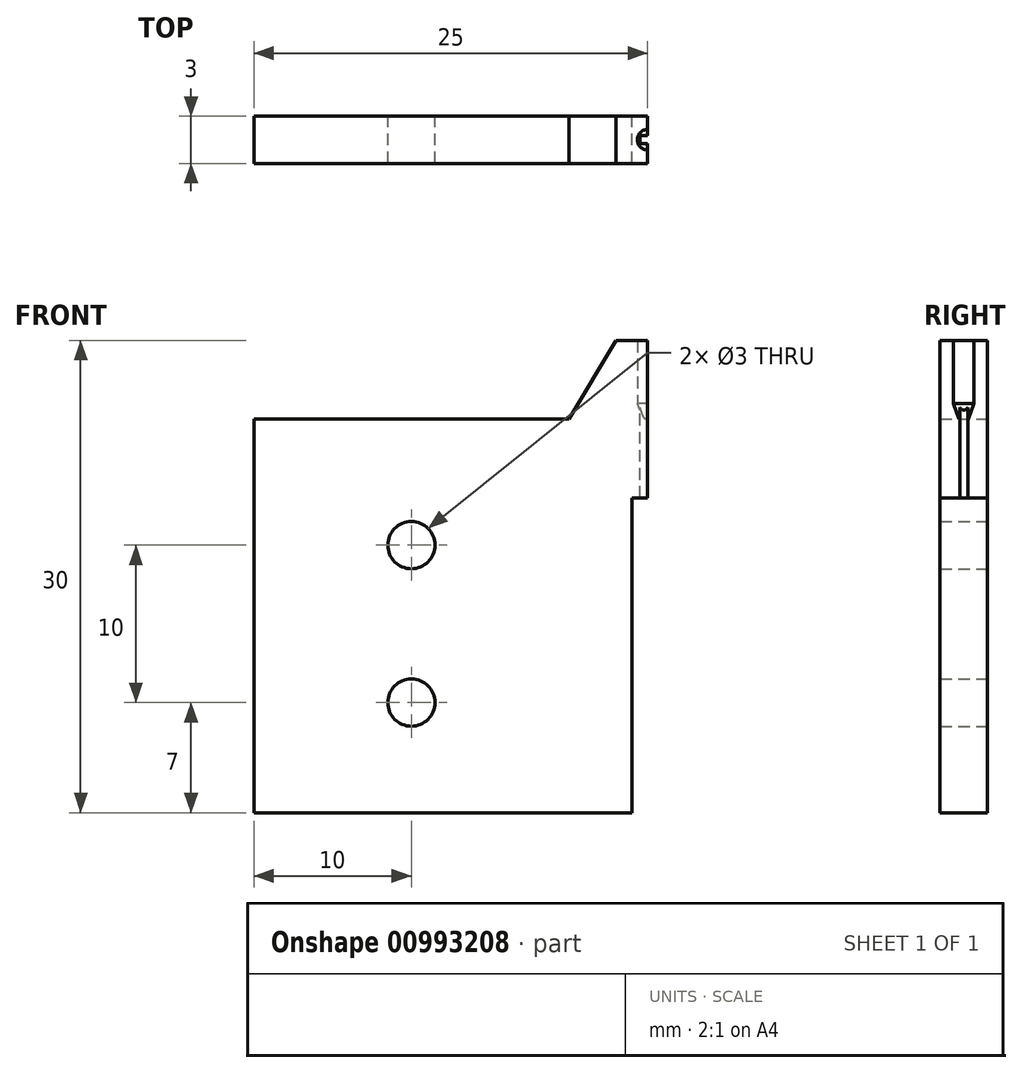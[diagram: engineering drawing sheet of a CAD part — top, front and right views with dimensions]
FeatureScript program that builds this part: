
annotation { "Feature Type Name" : "Feature", "Feature Type Description" : "" }
export const myFeature = defineFeature(function(context is Context, id is Id, definition is map)
    precondition{}
    {
        {
            var Q0;
            Q0=qCreatedBy(makeId("Front.planeOp"),FACE);
            var sketch = newSketch(context, id + "F0", { "sketchPlane" : qUnion([Q0])});
            skLineSegment(sketch, "E0.bottom", {"start": v(12.5, 15) * mm, "end": v(10.5, 15) * mm});
            skLineSegment(sketch, "E0.top", {"start": v(11.5, -15) * mm, "end": v(-12.5, -15) * mm});
            skLineSegment(sketch, "E0.left", {"start": v(12.5, 15) * mm, "end": v(12.5, 5) * mm});
            skLineSegment(sketch, "E0.right", {"start": v(-12.5, 10) * mm, "end": v(-12.5, -15) * mm});
            skPoint(sketch, "E0.middle", {"position": v(0, 0) * mm});
            skPoint(sketch, "E1.middle", {"position": v(-1, 12.5) * mm});
            skLineSegment(sketch, "E2.top", {"start": v(12.5, 5) * mm, "end": v(11.5, 5) * mm});
            skLineSegment(sketch, "E2.right", {"start": v(11.5, -15) * mm, "end": v(11.5, 5) * mm});
            skPoint(sketch, "E2.middle", {"position": v(12, -5) * mm});
            skPoint(sketch, "E3.orphan", {"position": v(-12.5, 15) * mm});
            skPoint(sketch, "E2.bottom.start.orphan", {"position": v(12.5, -15) * mm});
            skCircle(sketch, "E4", {"center": v(-2.5, -8) * mm, "radius": 1.5 * mm});
            skPoint(sketch, "E1.right.end.orphan", {"position": v(10.5, 10) * mm});
            skCircle(sketch, "E5", {"center": v(-2.5, 2) * mm, "radius": 1.5 * mm});
            skLineSegment(sketch, "E6", {"start": v(-12.5, 10) * mm, "end": v(7.5, 10) * mm});
            skLineSegment(sketch, "E7", {"start": v(7.5, 10) * mm, "end": v(10.5, 15) * mm});
            skSolve(sketch);
        }
        {
            var Q0;
            Q0=makeQuery(id+"F0.imprint","IMPRINT",FACE,{"disambiguationData":[TD([[makeQuery(id+"F0.imprint","IMPRINT",EDGE,{"derivedFrom":sQuery(id+"F0.wireOp",EDGE,"E0.bottom")}),1.0]])]});
            extrude(context, id + "F1", {"entities" : qUnion([Q0]), "depth" : 3 * mm, "offsetDistance" : 25 * mm});
        }
        {
            var Q0;
            Q0=makeQuery(id+"F1.opExtrude","SWEPT_FACE",FACE,{"disambiguationData":[OSD([sQuery(id+"F0.wireOp",EDGE,"E0.left")])]});
            var sketch = newSketch(context, id + "F2", { "sketchPlane" : qUnion([Q0])});
            skLineSegment(sketch, "E8", {"start": v(-1.5, 17) * mm, "end": v(-1.5, -10.16) * mm, "construction": true});
            skPoint(sketch, "E8.startSnap0", {"position": v(-1.5, 15) * mm});
            skLineSegment(sketch, "E9", {"start": v(-1.5, 15.88) * mm, "end": v(-0.85, 15.88) * mm});
            skLineSegment(sketch, "E10", {"start": v(-0.85, 15.88) * mm, "end": v(-0.85, 11) * mm});
            skLineSegment(sketch, "E11", {"start": v(-0.85, 11) * mm, "end": v(-1.2, 10) * mm});
            skLineSegment(sketch, "E12", {"start": v(-1.2, 10) * mm, "end": v(-1.5, 10) * mm});
            skLineSegment(sketch, "E13", {"start": v(-1.5, 15.88) * mm, "end": v(-1.5, 10) * mm});
            skSolve(sketch);
        }
        {
            var Q0;
            Q0 = qSketchRegion(id + "F2", true);
            var Q1;
            Q1=sQuery(id+"F2.wireOp",EDGE,"E8");
            revolve(context, id + "F3", {"operationType" : NewBodyOperationType.REMOVE, "surfaceOperationType" : NewSurfaceOperationType.NEW, "entities" : qUnion([Q0]), "axis" : qUnion([Q1]), "revolveType" : RevolveType.FULL, "oppositeDirection" : true});
        }
        {
            var Q0;
            Q0=makeQuery(id+"F1.opExtrude","SWEPT_FACE",FACE,{"disambiguationData":[OSD([sQuery(id+"F0.wireOp",EDGE,"E0.left")])]});
            var sketch = newSketch(context, id + "F4", { "sketchPlane" : qUnion([Q0])});
            skLineSegment(sketch, "E14.bottom", {"start": v(-1.25, 3.92) * mm, "end": v(-1.75, 3.92) * mm});
            skLineSegment(sketch, "E14.top", {"start": v(-1.25, 10.95) * mm, "end": v(-1.75, 10.95) * mm});
            skLineSegment(sketch, "E14.left", {"start": v(-1.25, 3.92) * mm, "end": v(-1.25, 10.95) * mm});
            skLineSegment(sketch, "E14.right", {"start": v(-1.75, 3.92) * mm, "end": v(-1.75, 10.95) * mm});
            skPoint(sketch, "E14.middle", {"position": v(-1.5, 7.43) * mm});
            skPoint(sketch, "E14.middle.positionSnap0", {"position": v(-1.5, 10) * mm});
            skPoint(sketch, "E14.centerSnap0", {"position": v(-1.5, 10) * mm});
            skSolve(sketch);
        }
        {
            var Q0;
            Q0 = qSketchRegion(id + "F4", true);
            extrude(context, id + "F5", {"entities" : qUnion([Q0]), "operationType" : NewBodyOperationType.REMOVE, "oppositeDirection" : true, "depth" : 0.5 * mm, "offsetDistance" : 25 * mm});
        }
    });
